# Revit family: Hager-Mini_Gamma-IP30-syst-BE-fr
name_source: partatom
category: Electrical Equipment
units: mm (PartAtom-declared; Revit-internal decimal feet)

## family parameters
Cut with Voids When Loaded = No
Host = Face
Panel Configuration = Two Columns, Circuits Across
Part Type = Panelboard
Room Calculation Point = No
Round Connector Dimension = Use Diameter
Shared = No

## types (9) — shared parameters
EF000003 - mode de pose = EV000384 - saillie
EF000007 - couleur = EV000202 - blanc
EF000049 - profondeur = 82 mm  [stored 0.269029 ft]
EF000116 - numéro RAL = 9010
EF000118 - avec cadre/support de montage = No
EF000266 - nombre de rangées = 1
EF001062 - finition CEM = No
EF001134 - rail DIN = No
EF001596 - matériau du boîtier/corps = EV000139 - plastique
EF004462 - type de fermeture = EV000154 - autre
EF005474 - indice de protection (IP) = EV006410 - IP30
EF006244 - couvercle/porte transparent(e) = No
EF006306 - avec serrure = No
EF009212 - finition du couvercle = EV009916 - avec échancrure
EF015941 - porte pour transmission du signal = No
HG000001 - nombre de colonnes = 1
HG000002 - avec porte = No
HG000003 - Gamme = Mini gamma
HG000005 - Epaisseur = 3 mm  [stored 0.00984252 ft]
HG000006 - Encastré = No
HG000009 - Porte à double battant = No
HG000010 - Portes asymétriques = No
HG000011 - Rangées du bas vides = No
HG000017 - Distance entre pôles = 18 mm  [stored 0.0590551 ft]
Manufacturer = Hager
Type Comments = Mini gamma
zero-valued in all types: Default Elevation, EF000218 - profondeur d'encastrement, EF000332 - hauteur d'encastrement, EF000846 - largeur d'encastrement, HG000007 - Nombre de colonnes vides, HG000008 - Nombre de rangées vides

## per-type parameters (varying)
| type | EF000008 - largeur | EF000040 - hauteur | EF000339 - type de capot | EF001088 - possibilité de montage en saillie | EF001131 - profondeur intérieure | EF002950 - largeur en nombre de modules | EF015776 - borne de mise à la terre | EF015777 - borne à conducteur neutre | HG000004 - Référence fabricant | Model |
| Saillie IP30 L110 H180 P82 4 Modules - GD104E | 110 mm | 180 mm | EV005746 - optionnel | No | 82 mm  [stored 0.269029 ft] | 4 | Yes | No | GD104E | GD104E |
| Saillie IP30 L110 H180 P82 4 Modules - GD104N | 110 mm | 180 mm | EV001012 - couvercle | No | 0 mm  [stored 0 ft] | 4 | Yes | Yes | GD104N | GD104N |
| Saillie IP30 L146 H180 P82 6 Modules - GD106E | 146 mm | 180 mm | EV005746 - optionnel | No | 82 mm  [stored 0.269029 ft] | 6 | Yes | No | GD106E | GD106E |
| Saillie IP30 L146 H180 P82 6 Modules - GD106N | 146 mm | 180 mm | EV005746 - optionnel | Yes | 82 mm  [stored 0.269029 ft] | 6 | Yes | Yes | GD106N | GD106N |
| Saillie IP30 L182 H180 P82 8 Modules - GD108E | 182 mm | 180 mm | EV005746 - optionnel | No | 82 mm  [stored 0.269029 ft] | 8 | Yes | No | GD108E | GD108E |
| Saillie IP30 L182 H180 P82 8 Modules - GD108N | 182 mm | 180 mm | EV005746 - optionnel | Yes | 82 mm  [stored 0.269029 ft] | 8 | Yes | Yes | GD108N | GD108N |
| Saillie IP30 L218 H180 P82 10 Modules - GD110E | 218 mm | 180 mm | EV005746 - optionnel | No | 82 mm  [stored 0.269029 ft] | 10 | Yes | No | GD110E | GD110E |
| Saillie IP30 L55 H160 P82 2 Modules - GD102E | 55 mm  [stored 0.180446 ft] | 160 mm  [stored 0.524934 ft] | EV005746 - optionnel | No | 82 mm  [stored 0.269029 ft] | 2 | No | No | GD102E | GD102E |
| Saillie IP30 L55 H160 P82 2 Modules - GD102N | 55 mm  [stored 0.180446 ft] | 160 mm  [stored 0.524934 ft] | EV005746 - optionnel | No | 82 mm  [stored 0.269029 ft] | 2 | No | No | GD102N | GD102N |

note: [stored X ft] marks values corroborated as IEEE doubles in the binary element streams (Revit-internal decimal feet)

## geometry (parser evidence)
native form markers: Sweep x17
no freeform markers — native parametric forms only
